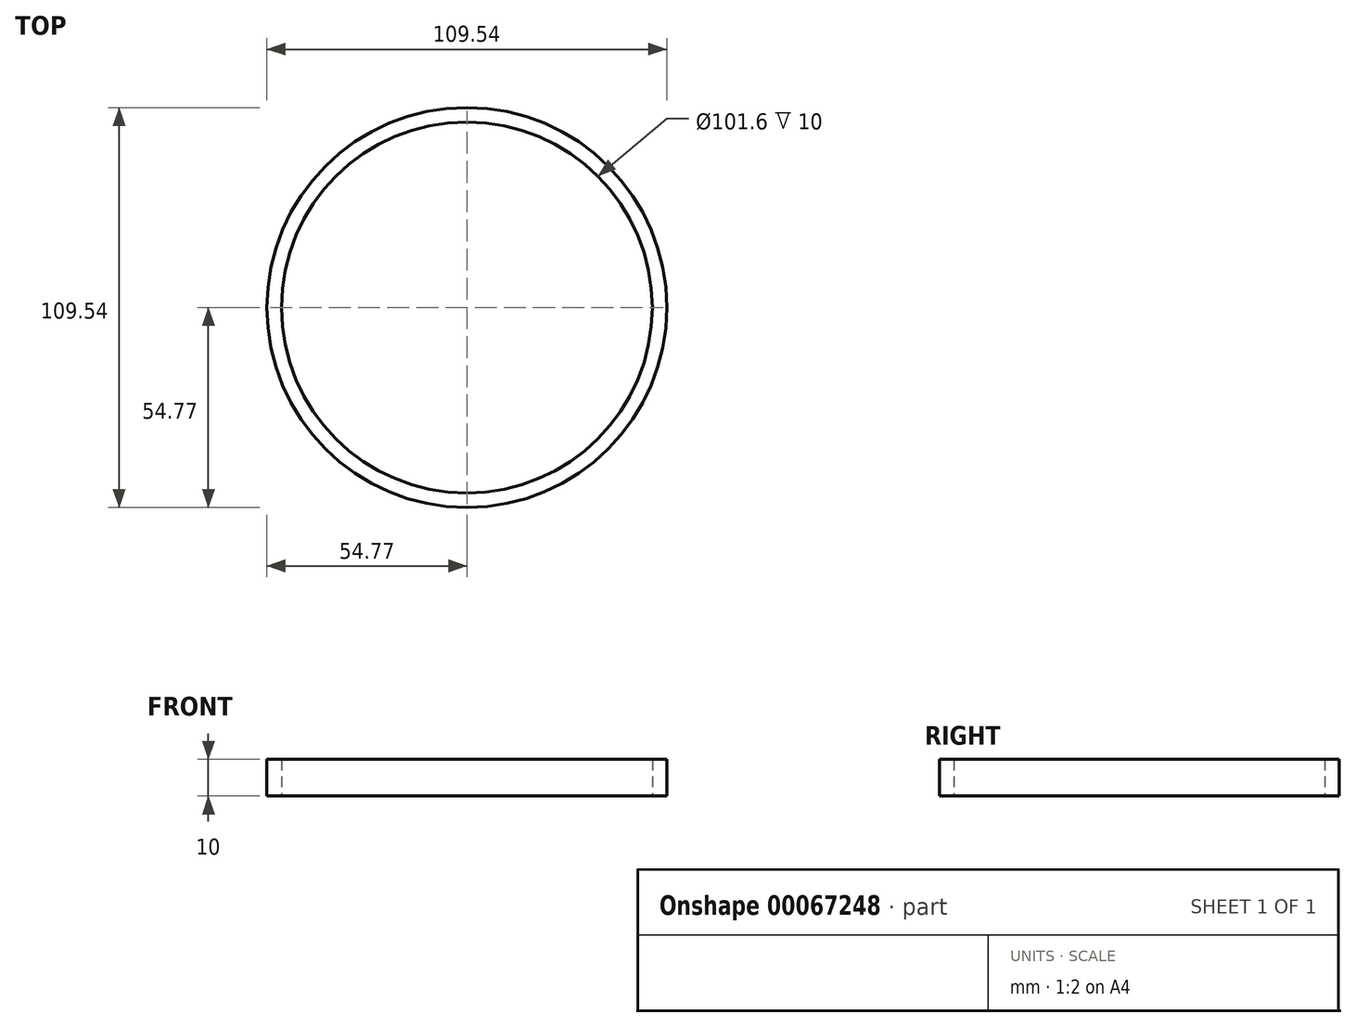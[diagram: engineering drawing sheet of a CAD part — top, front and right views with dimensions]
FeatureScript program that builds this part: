
annotation { "Feature Type Name" : "Feature", "Feature Type Description" : "" }
export const myFeature = defineFeature(function(context is Context, id is Id, definition is map)
    precondition{}
    {
        {
            var Q0;
            Q0=qCreatedBy(makeId("Top.planeOp"),FACE);
            var sketch = newSketch(context, id + "F0", { "sketchPlane" : qUnion([Q0])});
            skCircle(sketch, "E0", {"center": v(0, 0) * mm, "radius": 54.77 * mm});
            skCircle(sketch, "E1", {"center": v(0, 0) * mm, "radius": 50.8 * mm});
            skSolve(sketch);
        }
        {
            var Q0;
            Q0 = qSketchRegion(id + "F0", true);
            extrude(context, id + "F1", {"entities" : qUnion([Q0]), "depth" : 10 * mm});
        }
    });
